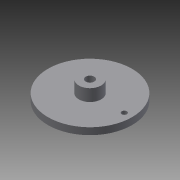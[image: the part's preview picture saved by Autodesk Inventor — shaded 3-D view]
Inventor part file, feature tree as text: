
AUTODESK INVENTOR PART (.ipt)
format: ipt  version: 2013 (Build 170138000, 138)  size: 86,016 bytes
history: native  units: mm
features: extrude x2, sketch x2
ambient origin geometry x8: Origin, YZ Plane, XZ Plane, XY Plane, X Axis, Y Axis, Z Axis, Center Point
bodies: Solid1 (feature_tree)
feature tree (4):
  extrude  "Extrusion1"  Depth=5.0mm
  extrude  "Extrusion2"  Depth=20.0mm
  sketch  "Sketch1"  dims[d0=49.0mm d1=5.0mm]
  sketch  "Sketch2"  dims[d2=3.0mm d3=20.0mm d4=4.0mm d5=0.0mm d6=13.0mm d7=7.0mm d8=0.0mm]
